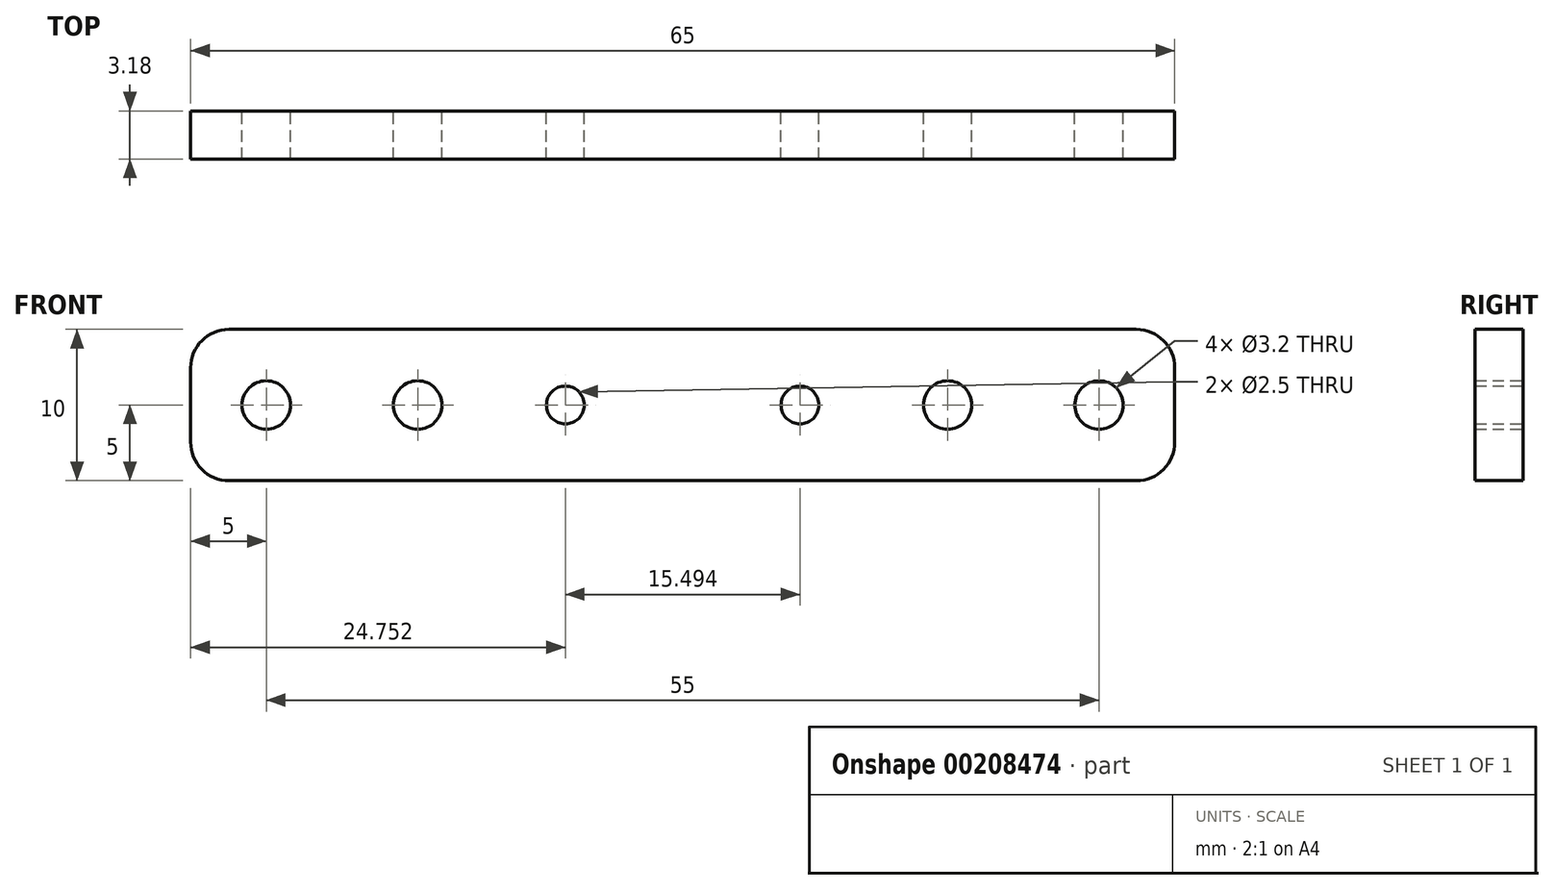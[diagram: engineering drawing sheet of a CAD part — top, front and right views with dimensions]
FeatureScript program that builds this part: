
annotation { "Feature Type Name" : "Feature", "Feature Type Description" : "" }
export const myFeature = defineFeature(function(context is Context, id is Id, definition is map)
    precondition{}
    {
        {
            var Q0;
            Q0=qCreatedBy(makeId("Front.planeOp"),FACE);
            var sketch = newSketch(context, id + "F0", { "sketchPlane" : qUnion([Q0])});
            skLineSegment(sketch, "E0.bottom", {"start": v(2.54, 0) * mm, "end": v(62.46, 0) * mm});
            skLineSegment(sketch, "E0.top", {"start": v(2.54, -10) * mm, "end": v(62.46, -10) * mm});
            skLineSegment(sketch, "E0.left", {"start": v(0, -2.54) * mm, "end": v(0, -7.46) * mm});
            skLineSegment(sketch, "E0.right", {"start": v(65, -2.54) * mm, "end": v(65, -7.46) * mm});
            skCircle(sketch, "E1", {"center": v(24.75, -5) * mm, "radius": 1.25 * mm});
            skCircle(sketch, "E2", {"center": v(40.25, -5) * mm, "radius": 1.25 * mm});
            skCircle(sketch, "E3", {"center": v(5, -5) * mm, "radius": 1.6 * mm});
            skCircle(sketch, "E4", {"center": v(15, -5) * mm, "radius": 1.6 * mm});
            skCircle(sketch, "E5", {"center": v(50, -5) * mm, "radius": 1.6 * mm});
            skCircle(sketch, "E6", {"center": v(60, -5) * mm, "radius": 1.6 * mm});
            skPoint(sketch, "E7.visualSharp", {"position": v(0, 0) * mm});
            skArc(sketch, "E7.filletArc", {"start": v(2.54, 0) * mm, "mid": v(0.74, -0.74) * mm, "end": v(0, -2.54) * mm});
            skPoint(sketch, "E8.visualSharp", {"position": v(0, -10) * mm});
            skArc(sketch, "E8.filletArc", {"start": v(0, -7.46) * mm, "mid": v(0.74, -9.26) * mm, "end": v(2.54, -10) * mm});
            skPoint(sketch, "E9.visualSharp", {"position": v(65, -10) * mm});
            skArc(sketch, "E9.filletArc", {"start": v(62.46, -10) * mm, "mid": v(64.26, -9.26) * mm, "end": v(65, -7.46) * mm});
            skPoint(sketch, "E10.visualSharp", {"position": v(65, 0) * mm});
            skArc(sketch, "E10.filletArc", {"start": v(65, -2.54) * mm, "mid": v(64.26, -0.74) * mm, "end": v(62.46, 0) * mm});
            skSolve(sketch);
        }
        {
            var Q0;
            Q0=makeQuery(id+"F0.imprint","IMPRINT",FACE,{"disambiguationData":[TD([[makeQuery(id+"F0.imprint","IMPRINT",EDGE,{"derivedFrom":sQuery(id+"F0.wireOp",EDGE,"E0.bottom")}),-1.0]])]});
            extrude(context, id + "F1", {"entities" : qUnion([Q0]), "depth" : 3.17 * mm});
        }
    });
